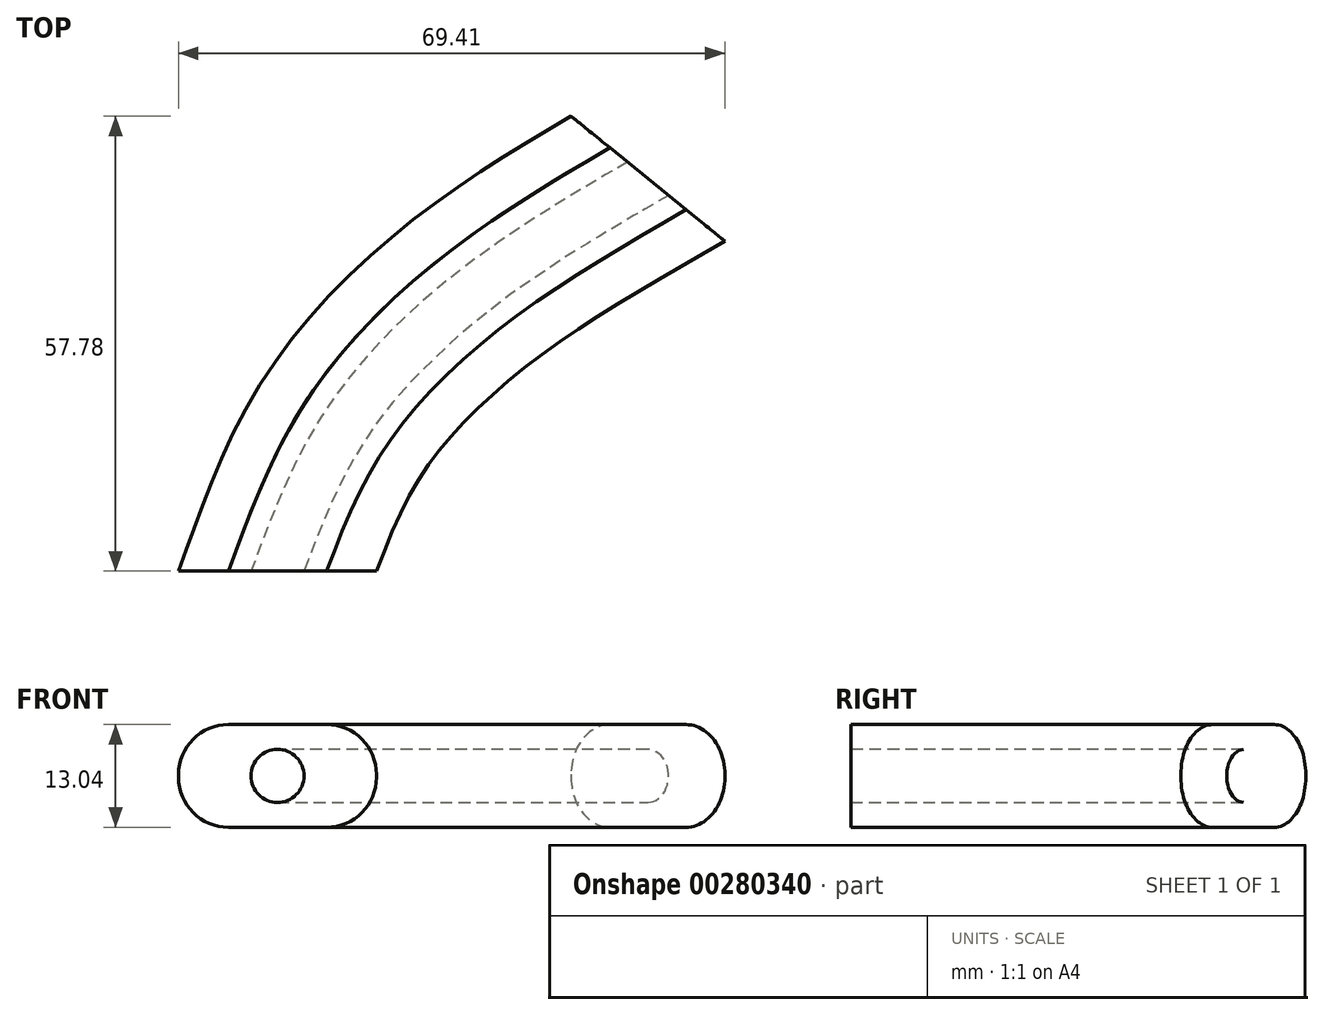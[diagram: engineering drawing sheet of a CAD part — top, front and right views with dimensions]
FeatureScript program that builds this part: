
annotation { "Feature Type Name" : "Feature", "Feature Type Description" : "" }
export const myFeature = defineFeature(function(context is Context, id is Id, definition is map)
    precondition{}
    {
        {
            var Q0;
            Q0=qCreatedBy(makeId("Top.planeOp"),FACE);
            var sketch = newSketch(context, id + "F0", { "sketchPlane" : qUnion([Q0])});
            skFitSpline(sketch, "E0", {"points": [v(0, 0) * mm, v(8.39, 18.17) * mm, v(24.7, 35.41) * mm, v(47.06, 49.85) * mm], "startDerivative": vector(22.62, 60.19) * mm, "endDerivative": vector(65.27, 38.2) * mm});
            skSolve(sketch);
        }
        {
            var Q0;
            Q0=qCreatedBy(makeId("Front.planeOp"),FACE);
            var sketch = newSketch(context, id + "F1", { "sketchPlane" : qUnion([Q0])});
            skLineSegment(sketch, "E1.bottom", {"start": v(-6.23, 6.52) * mm, "end": v(6.23, 6.52) * mm});
            skLineSegment(sketch, "E1.top", {"start": v(-6.23, -6.52) * mm, "end": v(6.23, -6.52) * mm});
            skLineSegment(sketch, "E1.left", {"start": v(-12.58, 0.17) * mm, "end": v(-12.58, -0.17) * mm});
            skLineSegment(sketch, "E1.right", {"start": v(12.58, 0.17) * mm, "end": v(12.58, -0.17) * mm});
            skPoint(sketch, "E1.middle", {"position": v(0, 0) * mm});
            skCircle(sketch, "E2", {"center": v(0, 0) * mm, "radius": 3.36 * mm});
            skPoint(sketch, "E3.visualSharp", {"position": v(-12.58, 6.52) * mm});
            skArc(sketch, "E3.filletArc", {"start": v(-6.23, 6.52) * mm, "mid": v(-10.72, 4.66) * mm, "end": v(-12.58, 0.17) * mm});
            skPoint(sketch, "E4.visualSharp", {"position": v(12.58, 6.52) * mm});
            skArc(sketch, "E4.filletArc", {"start": v(12.58, 0.17) * mm, "mid": v(10.72, 4.66) * mm, "end": v(6.23, 6.52) * mm});
            skPoint(sketch, "E5.visualSharp", {"position": v(-12.58, -6.52) * mm});
            skArc(sketch, "E5.filletArc", {"start": v(-12.58, -0.17) * mm, "mid": v(-10.72, -4.66) * mm, "end": v(-6.23, -6.52) * mm});
            skPoint(sketch, "E6.visualSharp", {"position": v(12.58, -6.52) * mm});
            skArc(sketch, "E6.filletArc", {"start": v(6.23, -6.52) * mm, "mid": v(10.72, -4.66) * mm, "end": v(12.58, -0.17) * mm});
            skSolve(sketch);
        }
        {
            var Q0;
            Q0=makeQuery(id+"F1.imprint","IMPRINT",FACE,{"disambiguationData":[TD([[makeQuery(id+"F1.imprint","IMPRINT",EDGE,{"derivedFrom":sQuery(id+"F1.wireOp",EDGE,"E1.bottom")}),-1.0]])]});
            var Q1;
            Q1=sQuery(id+"F0.wireOp",EDGE,"E0");
            sweep(context, id + "F2", {"profiles" : qUnion([Q0]), "path" : qUnion([Q1])});
        }
    });
